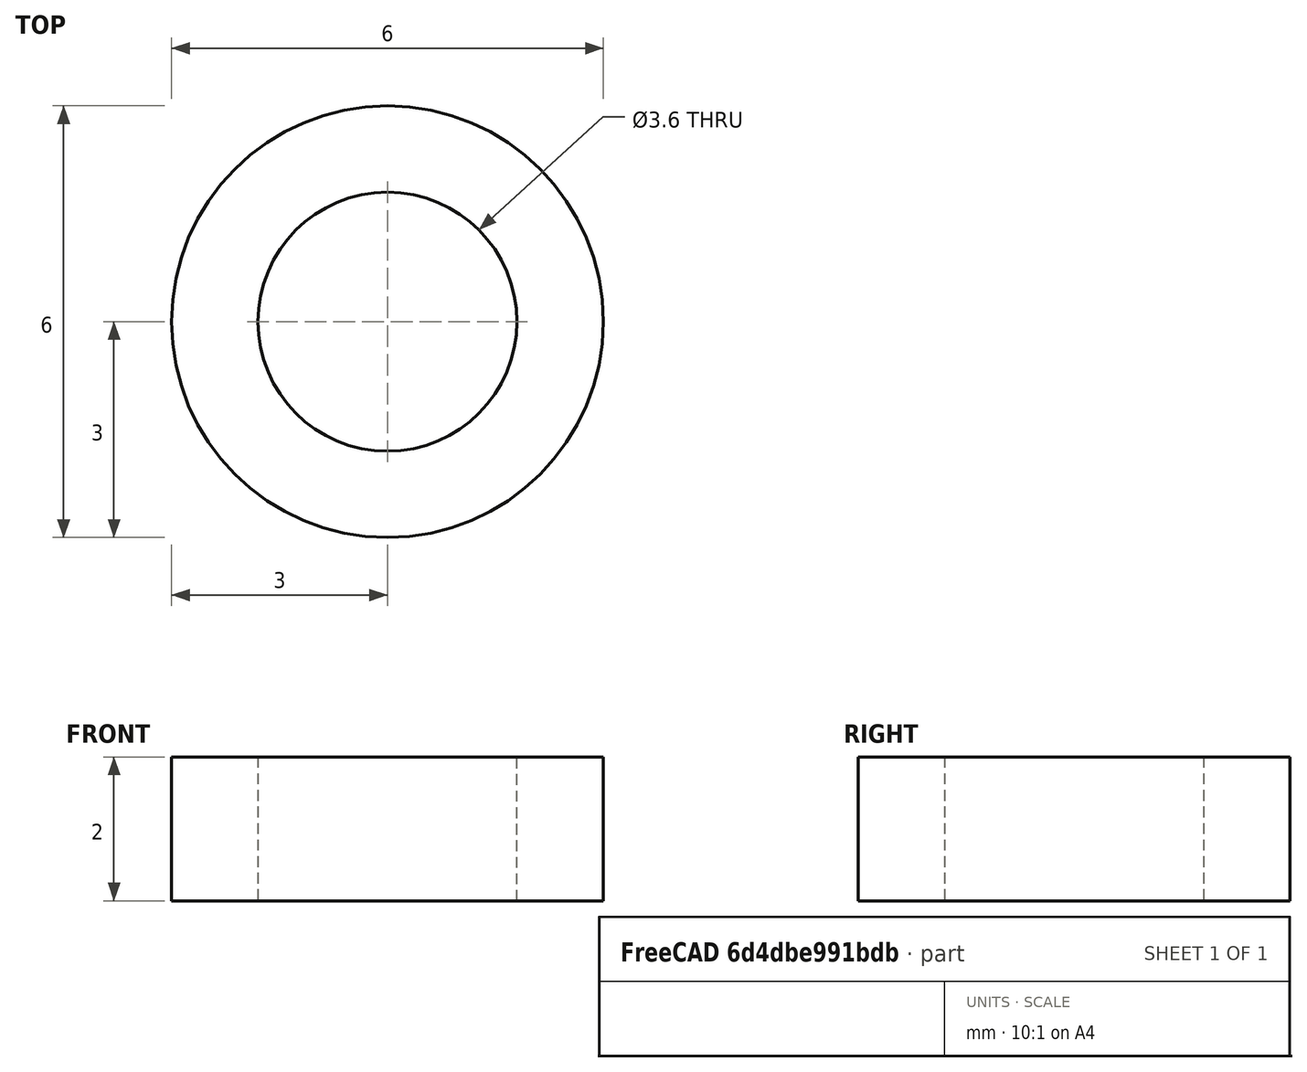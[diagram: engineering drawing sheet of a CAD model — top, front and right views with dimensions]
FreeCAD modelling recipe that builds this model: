
FCSTD DOCUMENT  (FreeCAD 0.19R24267 +99 (Git))
Label: outdoor_unit_case_LCD_Washers
License: All rights reserved
LicenseURL: http://en.wikipedia.org/wiki/All_rights_reserved
objects: Sketcher::SketchObject×1, PartDesign::Pad×1, PartDesign::Body×1
note: 4 computed .brp shape members not serialized (recipe doc carries the construction recipe); baked Part::Feature solids carry a one-line shape summary decoded from their .brp

FEATURE [Sketcher::SketchObject] Sketch
  FullyConstrained = true
  MapMode = 5
  Support = -> [XY_Plane]
  sketch-geometry (2):
    g0: Circle CenterX=0 CenterY=0 CenterZ=0 NormalX=0 NormalY=0 NormalZ=1 AngleXU=0 Radius=1.8
    g1: Circle CenterX=0 CenterY=0 CenterZ=0 NormalX=0 NormalY=0 NormalZ=1 AngleXU=0 Radius=3
  constraints (4):
    c: Coincident(g0,g-1)
    c: Coincident(g1,g0)
    c: Radius(g1) = 3
    c: Radius(g0) = 1.8
FEATURE [PartDesign::Pad] Pad
  Direction = (1,1,1)
  Length = 2
  Length2 = 100
  Profile = -> Sketch
  Type = 0
FEATURE [PartDesign::Body] Body
  Group = -> [Sketch,Pad]
  Origin = -> Origin
  Tip = -> Pad
